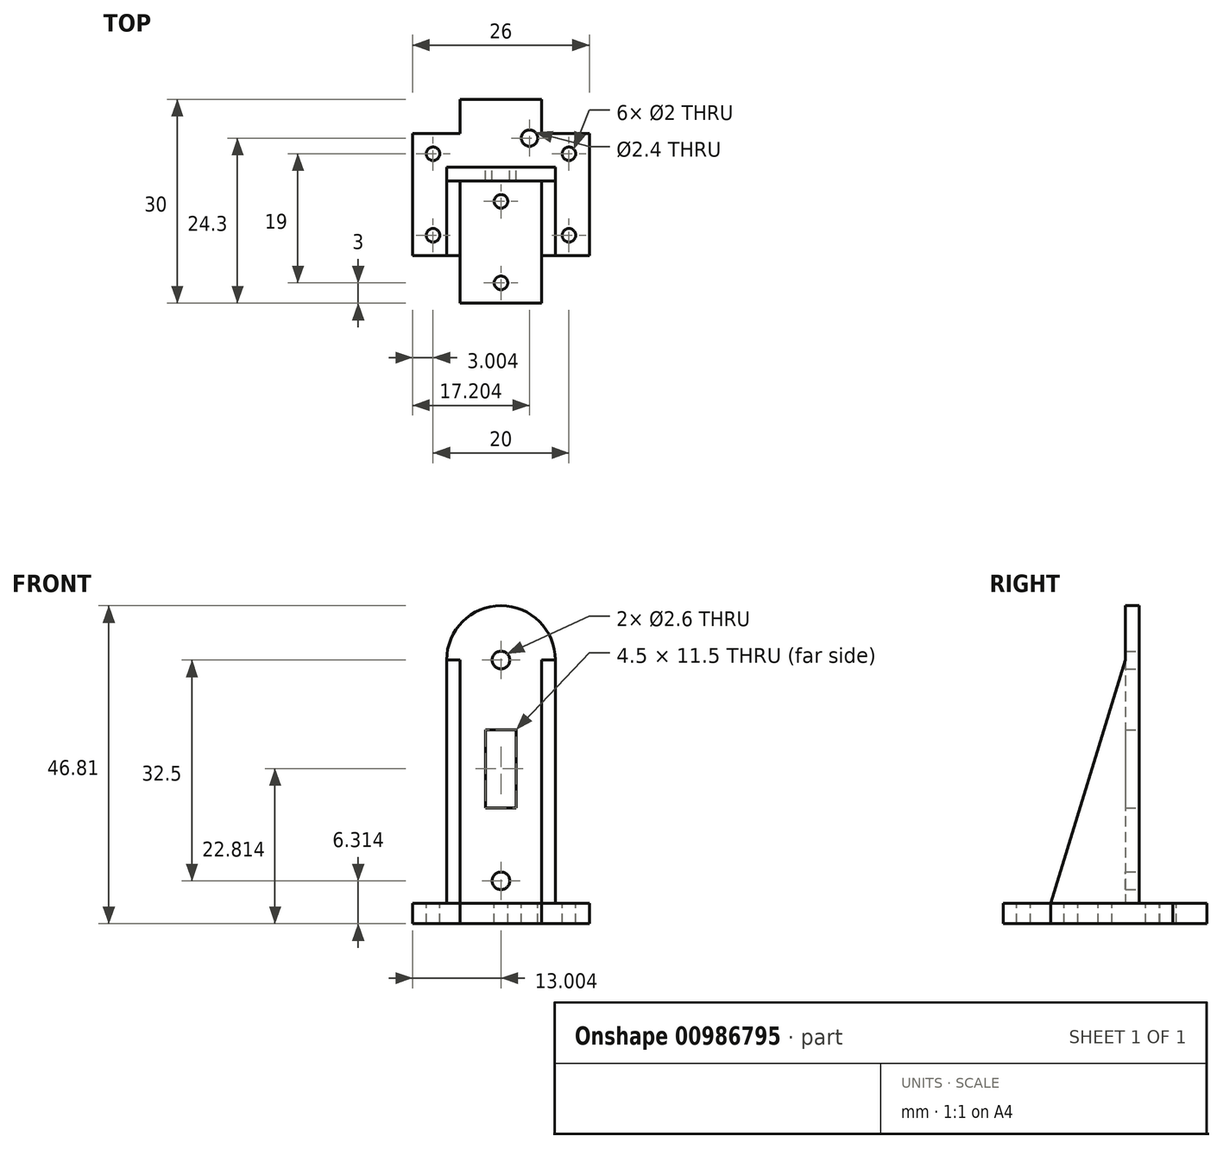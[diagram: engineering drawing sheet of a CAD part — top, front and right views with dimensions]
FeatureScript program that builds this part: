
annotation { "Feature Type Name" : "Feature", "Feature Type Description" : "" }
export const myFeature = defineFeature(function(context is Context, id is Id, definition is map)
    precondition{}
    {
        {
            var Q0;
            Q0=qCreatedBy(makeId("Front.planeOp"),FACE);
            var sketch = newSketch(context, id + "F0", { "sketchPlane" : qUnion([Q0])});
            skLineSegment(sketch, "E0.left", {"start": v(-16.93, 10) * mm, "end": v(-16.93, 42.5) * mm});
            skLineSegment(sketch, "E0.right", {"start": v(-28.93, 10) * mm, "end": v(-28.93, 42.5) * mm});
            skCircle(sketch, "E1", {"center": v(-22.93, 42.5) * mm, "radius": 1.3 * mm});
            skCircle(sketch, "E2", {"center": v(-22.93, 10) * mm, "radius": 1.3 * mm});
            skArc(sketch, "E3", {"start": v(-16.93, 42.5) * mm, "mid": v(-22.93, 48.5) * mm, "end": v(-28.93, 42.5) * mm});
            skLineSegment(sketch, "E4.top", {"start": v(-28.93, 6.68) * mm, "end": v(-16.93, 6.68) * mm});
            skLineSegment(sketch, "E4.left", {"start": v(-28.93, 10) * mm, "end": v(-28.93, 6.68) * mm});
            skLineSegment(sketch, "E4.right", {"start": v(-16.93, 10.68) * mm, "end": v(-16.93, 6.68) * mm});
            skLineSegment(sketch, "E5.bottom", {"start": v(-28.93, 6.68) * mm, "end": v(-16.94, 6.68) * mm});
            skLineSegment(sketch, "E5.top", {"start": v(-28.93, 3.68) * mm, "end": v(-16.94, 3.68) * mm});
            skLineSegment(sketch, "E5.left", {"start": v(-28.93, 6.68) * mm, "end": v(-28.93, 3.68) * mm});
            skLineSegment(sketch, "E5.right", {"start": v(-16.94, 6.68) * mm, "end": v(-16.94, 3.68) * mm});
            skSolve(sketch);
        }
        {
            var Q0;
            {var subQ0=sQuery(id+"F0.wireOp",EDGE,"E0.left");Q0=makeQuery(id+"F0.imprint","IMPRINT",FACE,{"disambiguationData":[TD([[makeQuery(id+"F0.imprint","IMPRINT",EDGE,{"derivedFrom":subQ0}),1.0]])]});}
            extrude(context, id + "F1", {"entities" : qUnion([Q0]), "depth" : 2 * mm, "offsetDistance" : 25 * mm});
        }
        {
            var Q0;
            Q0=makeQuery(id+"F1.opExtrude","CAP_FACE",FACE,{"disambiguationData":[OSD([sQuery(id+"F0.wireOp",EDGE,"E0.left"),sQuery(id+"F0.wireOp",EDGE,"E0.right"),sQuery(id+"F0.wireOp",EDGE,"E1"),sQuery(id+"F0.wireOp",EDGE,"E2"),sQuery(id+"F0.wireOp",EDGE,"E3"),sQuery(id+"F0.wireOp",EDGE,"E4.top"),sQuery(id+"F0.wireOp",EDGE,"E4.left"),sQuery(id+"F0.wireOp",EDGE,"E4.right"),sQuery(id+"F0.wireOp",EDGE,"E5.bottom")])],"isStart":false});
            var sketch = newSketch(context, id + "F2", { "sketchPlane" : qUnion([Q0])});
            skLineSegment(sketch, "E6.bottom", {"start": v(-28.93, 6.68) * mm, "end": v(-16.93, 6.68) * mm});
            skLineSegment(sketch, "E6.top", {"start": v(-28.93, 3.68) * mm, "end": v(-16.93, 3.68) * mm});
            skLineSegment(sketch, "E6.left", {"start": v(-28.93, 6.68) * mm, "end": v(-28.93, 3.68) * mm});
            skLineSegment(sketch, "E6.right", {"start": v(-16.93, 6.68) * mm, "end": v(-16.93, 3.68) * mm});
            skSolve(sketch);
        }
        {
            var Q0;
            Q0=makeQuery(id+"F2.imprint","IMPRINT",FACE,{"disambiguationData":[TD([[makeQuery(id+"F2.imprint","IMPRINT",EDGE,{"derivedFrom":sQuery(id+"F2.wireOp",EDGE,"E6.bottom")}),-1.0]])]});
            extrude(context, id + "F3", {"entities" : qUnion([Q0]), "operationType" : NewBodyOperationType.ADD, "depth" : 18 * mm, "offsetDistance" : 25 * mm, "hasSecondDirection" : true, "secondDirectionOppositeDirection" : true, "secondDirectionDepth" : 12 * mm});
        }
        {
            var Q0;
            Q0=makeQuery(id+"F3.boolean.opBoolean","MERGE",FACE,{"derivedFrom":[makeQuery(id+"F1.opExtrude","SWEPT_FACE",FACE,{"disambiguationData":[OSD([sQuery(id+"F0.wireOp",EDGE,"E0.left"),sQuery(id+"F0.wireOp",EDGE,"E4.right")])]}),makeQuery(id+"F3.opExtrude","SWEPT_FACE",FACE,{"disambiguationData":[OSD([sQuery(id+"F2.wireOp",EDGE,"E6.right")])]})]});
            var sketch = newSketch(context, id + "F4", { "sketchPlane" : qUnion([Q0])});
            skLineSegment(sketch, "E7.bottom", {"start": v(5, 6.68) * mm, "end": v(-13, 6.68) * mm});
            skLineSegment(sketch, "E7.top", {"start": v(5, 3.68) * mm, "end": v(-13, 3.68) * mm});
            skLineSegment(sketch, "E7.left", {"start": v(5, 6.68) * mm, "end": v(5, 3.68) * mm});
            skLineSegment(sketch, "E7.right", {"start": v(-13, 6.68) * mm, "end": v(-13, 3.68) * mm});
            skLineSegment(sketch, "E8", {"start": v(-13, 6.68) * mm, "end": v(-2, 42.5) * mm});
            skLineSegment(sketch, "E9", {"start": v(-2, 42.5) * mm, "end": v(0, 42.5) * mm});
            skLineSegment(sketch, "E10", {"start": v(0, 42.5) * mm, "end": v(0, 3.68) * mm});
            skSolve(sketch);
        }
        {
            var Q0;
            {var subQ4=sQuery(id+"F4.wireOp",EDGE,"E8");Q0=makeQuery(id+"F4.imprint","IMPRINT",FACE,{"disambiguationData":[TD([[makeQuery(id+"F4.imprint","IMPRINT",EDGE,{"derivedFrom":subQ4}),-1.0]])]});}
            var Q1;
            {var subQ0=sQuery(id+"F4.wireOp",EDGE,"E7.right");Q1=makeQuery(id+"F4.imprint","IMPRINT",FACE,{"disambiguationData":[TD([[makeQuery(id+"F4.imprint","IMPRINT",EDGE,{"derivedFrom":subQ0}),1.0]])]});}
            var Q2;
            {var subQ3=sQuery(id+"F4.wireOp",EDGE,"E7.left");Q2=makeQuery(id+"F4.imprint","IMPRINT",FACE,{"disambiguationData":[TD([[makeQuery(id+"F4.imprint","IMPRINT",EDGE,{"derivedFrom":subQ3}),-1.0]])]});}
            var Q3;
            {var subQ4=sQuery(id+"F4.wireOp",EDGE,"E9");Q3=makeQuery(id+"F4.imprint","IMPRINT",FACE,{"disambiguationData":[TD([[makeQuery(id+"F4.imprint","IMPRINT",EDGE,{"derivedFrom":subQ4}),-1.0]])]});}
            extrude(context, id + "F5", {"entities" : qUnion([Q0, Q1, Q2, Q3]), "operationType" : NewBodyOperationType.ADD, "depth" : 2 * mm, "offsetDistance" : 25 * mm});
        }
        {
            var Q0;
            Q0=makeQuery(id+"F3.boolean.opBoolean","MERGE",FACE,{"derivedFrom":[makeQuery(id+"F1.opExtrude","SWEPT_FACE",FACE,{"disambiguationData":[OSD([sQuery(id+"F0.wireOp",EDGE,"E0.right"),sQuery(id+"F0.wireOp",EDGE,"E4.left")])]}),makeQuery(id+"F3.opExtrude","SWEPT_FACE",FACE,{"disambiguationData":[OSD([sQuery(id+"F2.wireOp",EDGE,"E6.left")])]})]});
            var sketch = newSketch(context, id + "F6", { "sketchPlane" : qUnion([Q0])});
            skLineSegment(sketch, "E11.bottom", {"start": v(-5, 6.68) * mm, "end": v(13, 6.68) * mm});
            skLineSegment(sketch, "E11.top", {"start": v(-5, 3.68) * mm, "end": v(13, 3.68) * mm});
            skLineSegment(sketch, "E11.left", {"start": v(-5, 6.68) * mm, "end": v(-5, 3.68) * mm});
            skLineSegment(sketch, "E11.right", {"start": v(13, 6.68) * mm, "end": v(13, 3.68) * mm});
            skLineSegment(sketch, "E12", {"start": v(13, 6.68) * mm, "end": v(2, 42.5) * mm});
            skLineSegment(sketch, "E13", {"start": v(2, 42.5) * mm, "end": v(0, 42.5) * mm});
            skLineSegment(sketch, "E14", {"start": v(0, 42.5) * mm, "end": v(0, 6.68) * mm});
            skSolve(sketch);
        }
        {
            var Q0;
            Q0=makeQuery(id+"F6.imprint","IMPRINT",FACE,{"disambiguationData":[TD([[makeQuery(id+"F6.imprint","IMPRINT",EDGE,{"derivedFrom":sQuery(id+"F6.wireOp",EDGE,"E11.top")}),-1.0]])]});
            var Q1;
            {var subQ4=sQuery(id+"F6.wireOp",EDGE,"E12");Q1=makeQuery(id+"F6.imprint","IMPRINT",FACE,{"disambiguationData":[TD([[makeQuery(id+"F6.imprint","IMPRINT",EDGE,{"derivedFrom":subQ4}),1.0]])]});}
            var Q2;
            Q2=makeQuery(id+"F6.imprint","IMPRINT",FACE,{"disambiguationData":[TD([[makeQuery(id+"F6.imprint","IMPRINT",EDGE,{"derivedFrom":sQuery(id+"F6.wireOp",EDGE,"E13")}),1.0]])]});
            extrude(context, id + "F7", {"entities" : qUnion([Q0, Q1, Q2]), "operationType" : NewBodyOperationType.ADD, "depth" : 2 * mm, "offsetDistance" : 25 * mm});
        }
        {
            var Q0;
            Q0=makeQuery(id+"F7.opExtrude","CAP_FACE",FACE,{"disambiguationData":[OSD([sQuery(id+"F6.wireOp",EDGE,"E11.bottom"),sQuery(id+"F6.wireOp",EDGE,"E11.top"),sQuery(id+"F6.wireOp",EDGE,"E11.left"),sQuery(id+"F6.wireOp",EDGE,"E11.right"),sQuery(id+"F6.wireOp",EDGE,"E12"),sQuery(id+"F6.wireOp",EDGE,"E13"),sQuery(id+"F6.wireOp",EDGE,"E14")])],"isStart":false});
            var sketch = newSketch(context, id + "F8", { "sketchPlane" : qUnion([Q0])});
            skLineSegment(sketch, "E15.bottom", {"start": v(-5, 6.68) * mm, "end": v(13, 6.68) * mm});
            skLineSegment(sketch, "E15.top", {"start": v(-5, 3.68) * mm, "end": v(13, 3.68) * mm});
            skLineSegment(sketch, "E15.left", {"start": v(-5, 6.68) * mm, "end": v(-5, 3.68) * mm});
            skLineSegment(sketch, "E15.right", {"start": v(13, 6.68) * mm, "end": v(13, 3.68) * mm});
            skSolve(sketch);
        }
        {
            var Q0;
            Q0=makeQuery(id+"F8.imprint","IMPRINT",FACE,{"disambiguationData":[TD([[makeQuery(id+"F8.imprint","IMPRINT",EDGE,{"derivedFrom":sQuery(id+"F8.wireOp",EDGE,"E15.top")}),-1.0]])]});
            extrude(context, id + "F9", {"entities" : qUnion([Q0]), "operationType" : NewBodyOperationType.ADD, "depth" : 5 * mm, "offsetDistance" : 25 * mm});
        }
        {
            var Q0;
            Q0=makeQuery(id+"F5.opExtrude","CAP_FACE",FACE,{"disambiguationData":[OSD([sQuery(id+"F4.wireOp",EDGE,"E7.bottom"),sQuery(id+"F4.wireOp",EDGE,"E7.top"),sQuery(id+"F4.wireOp",EDGE,"E7.left"),sQuery(id+"F4.wireOp",EDGE,"E7.right"),sQuery(id+"F4.wireOp",EDGE,"E8"),sQuery(id+"F4.wireOp",EDGE,"E9"),sQuery(id+"F4.wireOp",EDGE,"E10")])],"isStart":false});
            var sketch = newSketch(context, id + "F10", { "sketchPlane" : qUnion([Q0])});
            skLineSegment(sketch, "E16.bottom", {"start": v(-13, 6.68) * mm, "end": v(5, 6.68) * mm});
            skLineSegment(sketch, "E16.top", {"start": v(-13, 3.68) * mm, "end": v(5, 3.68) * mm});
            skLineSegment(sketch, "E16.left", {"start": v(-13, 6.68) * mm, "end": v(-13, 3.68) * mm});
            skLineSegment(sketch, "E16.right", {"start": v(5, 6.68) * mm, "end": v(5, 3.68) * mm});
            skSolve(sketch);
        }
        {
            var Q0;
            Q0=makeQuery(id+"F10.imprint","IMPRINT",FACE,{"disambiguationData":[TD([[makeQuery(id+"F10.imprint","IMPRINT",EDGE,{"derivedFrom":sQuery(id+"F10.wireOp",EDGE,"E16.top")}),1.0]])]});
            extrude(context, id + "F11", {"entities" : qUnion([Q0]), "operationType" : NewBodyOperationType.ADD, "depth" : 5 * mm, "offsetDistance" : 25 * mm});
        }
        {
            var Q0;
            {var subQ0=sQuery(id+"F2.wireOp",EDGE,"E6.right");var subQ1=sQuery(id+"F2.wireOp",EDGE,"E6.left");var subQ2=sQuery(id+"F2.wireOp",EDGE,"E6.bottom");Q0=makeQuery(id+"F11.boolean.opBoolean","MERGE",FACE,{"derivedFrom":[makeQuery(id+"F9.boolean.opBoolean","MERGE",FACE,{"derivedFrom":[makeQuery(id+"F7.boolean.opBoolean","MERGE",FACE,{"derivedFrom":[makeQuery(id+"F5.boolean.opBoolean","MERGE",FACE,{"derivedFrom":[makeQuery(id+"F3.boolean.opBoolean","SPLIT",FACE,{"disambiguationData":[TD([makeQuery(id+"F3.opExtrude","CAP_FACE",FACE,{"disambiguationData":[OSD([subQ2,sQuery(id+"F2.wireOp",EDGE,"E6.top"),subQ1,subQ0])],"isStart":true})])],"derivedFrom":makeQuery(id+"F3.opExtrude","SWEPT_FACE",FACE,{"disambiguationData":[OSD([subQ2])]})}),makeQuery(id+"F5.opExtrude","SWEPT_FACE",FACE,{"disambiguationData":[OSD([sQuery(id+"F4.wireOp",EDGE,"E7.bottom")])]})]}),makeQuery(id+"F7.opExtrude","SWEPT_FACE",FACE,{"disambiguationData":[OSD([sQuery(id+"F6.wireOp",EDGE,"E11.bottom")])]})]}),makeQuery(id+"F9.opExtrude","SWEPT_FACE",FACE,{"disambiguationData":[OSD([sQuery(id+"F8.wireOp",EDGE,"E15.bottom")])]})]}),makeQuery(id+"F11.opExtrude","SWEPT_FACE",FACE,{"disambiguationData":[OSD([sQuery(id+"F10.wireOp",EDGE,"E16.bottom")])]})]});}
            var sketch = newSketch(context, id + "F12", { "sketchPlane" : qUnion([Q0])});
            skCircle(sketch, "E17", {"center": v(-22.93, 7) * mm, "radius": 1 * mm});
            skCircle(sketch, "E18", {"center": v(-32.93, 2) * mm, "radius": 1 * mm});
            skCircle(sketch, "E19", {"center": v(-12.93, 2) * mm, "radius": 1 * mm});
            skCircle(sketch, "E20", {"center": v(-12.93, -10) * mm, "radius": 1 * mm});
            skCircle(sketch, "E21", {"center": v(-32.93, -10) * mm, "radius": 1 * mm});
            skCircle(sketch, "E22", {"center": v(-22.93, -17) * mm, "radius": 1 * mm});
            skCircle(sketch, "E23", {"center": v(-22.93, -5) * mm, "radius": 1 * mm});
            skSolve(sketch);
        }
        {
            var Q0;
            Q0=makeQuery(id+"F12.imprint","IMPRINT",FACE,{"disambiguationData":[TD([[makeQuery(id+"F12.imprint","IMPRINT",EDGE,{"derivedFrom":sQuery(id+"F12.wireOp",EDGE,"E18")}),1.0]])]});
            var Q1;
            Q1=makeQuery(id+"F12.imprint","IMPRINT",FACE,{"disambiguationData":[TD([[makeQuery(id+"F12.imprint","IMPRINT",EDGE,{"derivedFrom":sQuery(id+"F12.wireOp",EDGE,"E19")}),1.0]])]});
            var Q2;
            Q2=makeQuery(id+"F12.imprint","IMPRINT",FACE,{"disambiguationData":[TD([[makeQuery(id+"F12.imprint","IMPRINT",EDGE,{"derivedFrom":sQuery(id+"F12.wireOp",EDGE,"E20")}),1.0]])]});
            var Q3;
            Q3=makeQuery(id+"F12.imprint","IMPRINT",FACE,{"disambiguationData":[TD([[makeQuery(id+"F12.imprint","IMPRINT",EDGE,{"derivedFrom":sQuery(id+"F12.wireOp",EDGE,"E23")}),1.0]])]});
            var Q4;
            Q4=makeQuery(id+"F12.imprint","IMPRINT",FACE,{"disambiguationData":[TD([[makeQuery(id+"F12.imprint","IMPRINT",EDGE,{"derivedFrom":sQuery(id+"F12.wireOp",EDGE,"E21")}),1.0]])]});
            var Q5;
            Q5=makeQuery(id+"F12.imprint","IMPRINT",FACE,{"disambiguationData":[TD([[makeQuery(id+"F12.imprint","IMPRINT",EDGE,{"derivedFrom":sQuery(id+"F12.wireOp",EDGE,"E22")}),1.0]])]});
            extrude(context, id + "F13", {"entities" : qUnion([Q0, Q1, Q2, Q3, Q4, Q5]), "operationType" : NewBodyOperationType.REMOVE, "oppositeDirection" : true, "depth" : 5 * mm, "offsetDistance" : 25 * mm});
        }
        {
            var Q0;
            Q0=makeQuery(id+"F7.boolean.opBoolean","MERGE",FACE,{"derivedFrom":[makeQuery(id+"F5.boolean.opBoolean","MERGE",FACE,{"derivedFrom":[makeQuery(id+"F1.opExtrude","CAP_FACE",FACE,{"disambiguationData":[OSD([sQuery(id+"F0.wireOp",EDGE,"E0.left"),sQuery(id+"F0.wireOp",EDGE,"E0.right"),sQuery(id+"F0.wireOp",EDGE,"E1"),sQuery(id+"F0.wireOp",EDGE,"E2"),sQuery(id+"F0.wireOp",EDGE,"E3"),sQuery(id+"F0.wireOp",EDGE,"E4.top"),sQuery(id+"F0.wireOp",EDGE,"E4.left"),sQuery(id+"F0.wireOp",EDGE,"E4.right"),sQuery(id+"F0.wireOp",EDGE,"E5.bottom")])],"isStart":true}),makeQuery(id+"F5.opExtrude","SWEPT_FACE",FACE,{"disambiguationData":[OSD([sQuery(id+"F4.wireOp",EDGE,"E10")])]})]}),makeQuery(id+"F7.opExtrude","SWEPT_FACE",FACE,{"disambiguationData":[OSD([sQuery(id+"F6.wireOp",EDGE,"E14")])]})]});
            var sketch = newSketch(context, id + "F14", { "sketchPlane" : qUnion([Q0])});
            skLineSegment(sketch, "E24", {"start": v(22.93, 10) * mm, "end": v(22.93, 42.5) * mm});
            skLineSegment(sketch, "E25.bottom", {"start": v(20.68, 20.74) * mm, "end": v(25.18, 20.74) * mm});
            skLineSegment(sketch, "E25.top", {"start": v(20.68, 32.24) * mm, "end": v(25.18, 32.24) * mm});
            skLineSegment(sketch, "E25.left", {"start": v(20.68, 20.74) * mm, "end": v(20.68, 32.24) * mm});
            skLineSegment(sketch, "E25.right", {"start": v(25.18, 20.74) * mm, "end": v(25.18, 32.24) * mm});
            skSolve(sketch);
        }
        {
            var Q0;
            {var subQ5=sQuery(id+"F14.wireOp",EDGE,"E25.right");Q0=makeQuery(id+"F14.imprint","IMPRINT",FACE,{"disambiguationData":[TD([[makeQuery(id+"F14.imprint","IMPRINT",EDGE,{"derivedFrom":subQ5}),1.0]])]});}
            var Q1;
            {var subQ5=sQuery(id+"F14.wireOp",EDGE,"E25.left");Q1=makeQuery(id+"F14.imprint","IMPRINT",FACE,{"disambiguationData":[TD([[makeQuery(id+"F14.imprint","IMPRINT",EDGE,{"derivedFrom":subQ5}),-1.0]])]});}
            extrude(context, id + "F15", {"entities" : qUnion([Q0, Q1]), "operationType" : NewBodyOperationType.REMOVE, "oppositeDirection" : true, "depth" : 3 * mm, "offsetDistance" : 25 * mm});
        }
        {
            var Q0;
            {var subQ0=sQuery(id+"F2.wireOp",EDGE,"E6.right");var subQ1=sQuery(id+"F2.wireOp",EDGE,"E6.left");var subQ2=sQuery(id+"F2.wireOp",EDGE,"E6.bottom");Q0=makeQuery(id+"F3.boolean.opBoolean","SPLIT",FACE,{"disambiguationData":[TD([makeQuery(id+"F3.opExtrude","CAP_FACE",FACE,{"disambiguationData":[OSD([subQ2,sQuery(id+"F2.wireOp",EDGE,"E6.top"),subQ1,subQ0])],"isStart":false})])],"derivedFrom":makeQuery(id+"F3.opExtrude","SWEPT_FACE",FACE,{"disambiguationData":[OSD([subQ2])]})});}
            var sketch = newSketch(context, id + "F16", { "sketchPlane" : qUnion([Q0])});
            skCircle(sketch, "E26", {"center": v(-18.73, 4.3) * mm, "radius": 1.2 * mm});
            skLineSegment(sketch, "E27", {"start": v(-22.93, 10.03) * mm, "end": v(-22.93, 1.3) * mm});
            skSolve(sketch);
        }
        {
            var Q0;
            Q0=makeQuery(id+"F16.imprint","IMPRINT",FACE,{"disambiguationData":[TD([[makeQuery(id+"F16.imprint","IMPRINT",EDGE,{"derivedFrom":sQuery(id+"F16.wireOp",EDGE,"E26")}),1.0]])]});
            extrude(context, id + "F17", {"entities" : qUnion([Q0]), "operationType" : NewBodyOperationType.REMOVE, "oppositeDirection" : true, "depth" : 3 * mm, "offsetDistance" : 25 * mm});
        }
        {
            var Q0;
            Q0=makeQuery(id+"F7.boolean.opBoolean","MERGE",FACE,{"derivedFrom":[makeQuery(id+"F5.boolean.opBoolean","MERGE",FACE,{"derivedFrom":[makeQuery(id+"F1.opExtrude","CAP_FACE",FACE,{"disambiguationData":[OSD([sQuery(id+"F0.wireOp",EDGE,"E0.left"),sQuery(id+"F0.wireOp",EDGE,"E0.right"),sQuery(id+"F0.wireOp",EDGE,"E1"),sQuery(id+"F0.wireOp",EDGE,"E2"),sQuery(id+"F0.wireOp",EDGE,"E3"),sQuery(id+"F0.wireOp",EDGE,"E4.top"),sQuery(id+"F0.wireOp",EDGE,"E4.left"),sQuery(id+"F0.wireOp",EDGE,"E4.right"),sQuery(id+"F0.wireOp",EDGE,"E5.bottom")])],"isStart":true}),makeQuery(id+"F5.opExtrude","SWEPT_FACE",FACE,{"disambiguationData":[OSD([sQuery(id+"F4.wireOp",EDGE,"E10")])]})]}),makeQuery(id+"F7.opExtrude","SWEPT_FACE",FACE,{"disambiguationData":[OSD([sQuery(id+"F6.wireOp",EDGE,"E14")])]})]});
            var sketch = newSketch(context, id + "F18", { "sketchPlane" : qUnion([Q0])});
            skArc(sketch, "E28", {"start": v(30.93, 42.5) * mm, "mid": v(22.93, 50.5) * mm, "end": v(14.93, 42.5) * mm});
            skSolve(sketch);
        }
        {
            var Q0;
            Q0=makeQuery(id+"F18.imprint","IMPRINT",FACE,{"disambiguationData":[TD([[makeQuery(id+"F18.imprint","IMPRINT",EDGE,{"derivedFrom":sQuery(id+"F18.wireOp",EDGE,"E28")}),1.0]])]});
            extrude(context, id + "F19", {"entities" : qUnion([Q0]), "operationType" : NewBodyOperationType.ADD, "oppositeDirection" : true, "depth" : 2 * mm, "offsetDistance" : 25 * mm});
        }
    });
